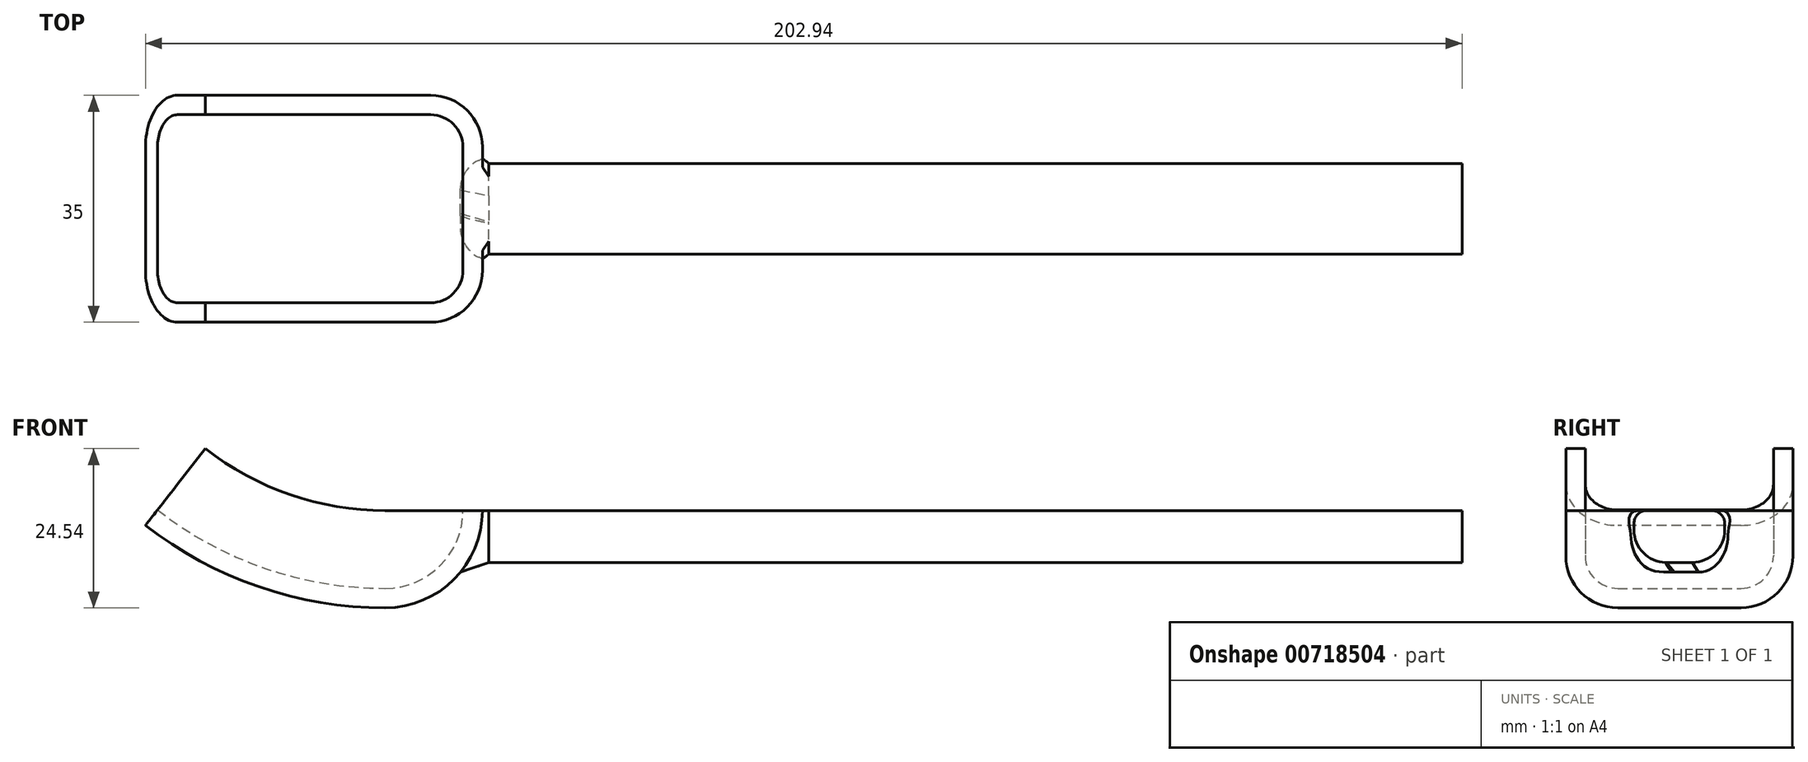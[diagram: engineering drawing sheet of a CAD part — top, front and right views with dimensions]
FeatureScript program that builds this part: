
annotation { "Feature Type Name" : "Feature", "Feature Type Description" : "" }
export const myFeature = defineFeature(function(context is Context, id is Id, definition is map)
    precondition{}
    {
        {
            assignVariable(context, id + "F0", {"variableType" : VariableType.ANGLE, "name" : "Rotation", "angleValue" : 38 * degree});
        }
        {
            assignVariable(context, id + "F1", {"variableType" : VariableType.LENGTH, "name" : "HandleLength", "lengthValue" : 150 * mm});
        }
        {
            assignVariable(context, id + "F2", {"variableType" : VariableType.LENGTH, "name" : "HandleStart", "lengthValue" : 16 * mm});
        }
        {
            var Q0;
            Q0=qCreatedBy(makeId("Right.planeOp"),FACE);
            var sketch = newSketch(context, id + "F3", { "sketchPlane" : qUnion([Q0])});
            skLineSegment(sketch, "E0", {"start": v(0, 0) * mm, "end": v(9.5, 0) * mm});
            skLineSegment(sketch, "E1", {"start": v(0, 0) * mm, "end": v(-9.5, 0) * mm});
            skLineSegment(sketch, "E2", {"start": v(-17.5, 8) * mm, "end": v(-17.5, 15) * mm});
            skLineSegment(sketch, "E3", {"start": v(-17.5, 15) * mm, "end": v(-14.5, 15) * mm});
            skLineSegment(sketch, "E4", {"start": v(-14.5, 15) * mm, "end": v(-14.5, 8) * mm});
            skLineSegment(sketch, "E5", {"start": v(-9.5, 3) * mm, "end": v(9.5, 3) * mm});
            skLineSegment(sketch, "E6", {"start": v(14.5, 8) * mm, "end": v(14.5, 15) * mm});
            skLineSegment(sketch, "E7", {"start": v(14.5, 15) * mm, "end": v(17.5, 15) * mm});
            skLineSegment(sketch, "E8", {"start": v(17.5, 15) * mm, "end": v(17.5, 8) * mm});
            skPoint(sketch, "E9.visualSharp", {"position": v(-14.5, 3) * mm});
            skArc(sketch, "E9.filletArc", {"start": v(-14.5, 8) * mm, "mid": v(-13.04, 4.46) * mm, "end": v(-9.5, 3) * mm});
            skPoint(sketch, "E10.visualSharp", {"position": v(14.5, 3) * mm});
            skArc(sketch, "E10.filletArc", {"start": v(9.5, 3) * mm, "mid": v(13.04, 4.46) * mm, "end": v(14.5, 8) * mm});
            skPoint(sketch, "E11.visualSharp", {"position": v(17.5, 0) * mm});
            skArc(sketch, "E11.filletArc", {"start": v(9.5, 0) * mm, "mid": v(15.16, 2.34) * mm, "end": v(17.5, 8) * mm});
            skPoint(sketch, "E12.visualSharp", {"position": v(-17.5, 0) * mm});
            skArc(sketch, "E12.filletArc", {"start": v(-17.5, 8) * mm, "mid": v(-15.16, 2.34) * mm, "end": v(-9.5, 0) * mm});
            skLineSegment(sketch, "E13", {"start": v(-13.2, 60) * mm, "end": v(15.15, 60) * mm});
            skSolve(sketch);
        }
        {
            var Q0;
            Q0=makeQuery(id+"F3.imprint","IMPRINT",FACE,{"disambiguationData":[TD([[makeQuery(id+"F3.imprint","IMPRINT",EDGE,{"derivedFrom":sQuery(id+"F3.wireOp",EDGE,"E0")}),1.0]])]});
            var Q1;
            Q1=sQuery(id+"F3.wireOp",EDGE,"E13");
            revolve(context, id + "F4", {"surfaceOperationType" : NewSurfaceOperationType.NEW, "entities" : qUnion([Q0]), "axis" : qUnion([Q1]), "revolveType" : RevolveType.ONE_DIRECTION, "angle" : getVariable(context, 'Rotation')});
        }
        {
            var Q0;
            Q0=makeQuery(id+"F4.opRevolve","CAP_FACE",FACE,{"disambiguationData":[OSD([sQuery(id+"F3.wireOp",EDGE,"E0"),sQuery(id+"F3.wireOp",EDGE,"E1"),sQuery(id+"F3.wireOp",EDGE,"E2"),sQuery(id+"F3.wireOp",EDGE,"E3"),sQuery(id+"F3.wireOp",EDGE,"E4"),sQuery(id+"F3.wireOp",EDGE,"E5"),sQuery(id+"F3.wireOp",EDGE,"E6"),sQuery(id+"F3.wireOp",EDGE,"E7"),sQuery(id+"F3.wireOp",EDGE,"E8"),sQuery(id+"F3.wireOp",EDGE,"E9.filletArc"),sQuery(id+"F3.wireOp",EDGE,"E10.filletArc"),sQuery(id+"F3.wireOp",EDGE,"E11.filletArc"),sQuery(id+"F3.wireOp",EDGE,"E12.filletArc")])],"isStart":true});
            var Q1;
            Q1=makeQuery(id+"F4.opRevolve","CAP_EDGE",EDGE,{"disambiguationData":[OSD([sQuery(id+"F3.wireOp",EDGE,"E3")])],"isStart":true});
            revolve(context, id + "F5", {"operationType" : NewBodyOperationType.ADD, "surfaceOperationType" : NewSurfaceOperationType.NEW, "entities" : qUnion([Q0]), "axis" : qUnion([Q1]), "revolveType" : RevolveType.ONE_DIRECTION, "oppositeDirection" : true, "angle" : 90 * degree});
        }
        {
            var Q0;
            Q0=qCreatedBy(makeId("Right.planeOp"),FACE);
            cPlane(context, id + "F6", {"entities" : qUnion([Q0]), "cplaneType" : CPlaneType.OFFSET, "offset" : getVariable(context, 'HandleStart'), "width" : 150 * mm, "height" : 150 * mm});
        }
        {
            var Q0;
            Q0=qCreatedBy(id+"F6.planeOp",FACE);
            var sketch = newSketch(context, id + "F7", { "sketchPlane" : qUnion([Q0])});
            skLineSegment(sketch, "E14", {"start": v(0, 15) * mm, "end": v(5, 15) * mm});
            skLineSegment(sketch, "E15", {"start": v(7, 13) * mm, "end": v(7, 12) * mm});
            skLineSegment(sketch, "E16", {"start": v(2, 7) * mm, "end": v(-2, 7) * mm});
            skLineSegment(sketch, "E17", {"start": v(-7, 12) * mm, "end": v(-7, 13) * mm});
            skLineSegment(sketch, "E18", {"start": v(-5, 15) * mm, "end": v(0, 15) * mm});
            skPoint(sketch, "E19.visualSharp", {"position": v(-7, 15) * mm});
            skArc(sketch, "E19.filletArc", {"start": v(-5, 15) * mm, "mid": v(-6.41, 14.41) * mm, "end": v(-7, 13) * mm});
            skPoint(sketch, "E20.visualSharp", {"position": v(7, 15) * mm});
            skArc(sketch, "E20.filletArc", {"start": v(7, 13) * mm, "mid": v(6.41, 14.41) * mm, "end": v(5, 15) * mm});
            skPoint(sketch, "E21.visualSharp", {"position": v(7, 7) * mm});
            skArc(sketch, "E21.filletArc", {"start": v(2, 7) * mm, "mid": v(5.54, 8.46) * mm, "end": v(7, 12) * mm});
            skPoint(sketch, "E22.visualSharp", {"position": v(-7, 7) * mm});
            skArc(sketch, "E22.filletArc", {"start": v(-7, 12) * mm, "mid": v(-5.54, 8.46) * mm, "end": v(-2, 7) * mm});
            skSolve(sketch);
        }
        {
            var Q0;
            Q0=makeQuery(id+"F5.opRevolve","CAP_EDGE",EDGE,{"disambiguationData":[OSD([sQuery(id+"F3.wireOp",EDGE,"E0"),sQuery(id+"F3.wireOp",EDGE,"E1")])],"isStart":false});
            cPlane(context, id + "F8", {"entities" : qUnion([Q0]), "cplaneType" : CPlaneType.LINE_ANGLE, "offset" : 25 * mm, "angle" : 60 * degree, "width" : 150 * mm, "height" : 150 * mm});
        }
        {
            var Q0;
            Q0=qCreatedBy(id+"F8.planeOp",FACE);
            var sketch = newSketch(context, id + "F9", { "sketchPlane" : qUnion([Q0])});
            skLineSegment(sketch, "E23", {"start": v(0, 8.5) * mm, "end": v(3.4, 8.5) * mm});
            skLineSegment(sketch, "E24", {"start": v(8.4, 13.5) * mm, "end": v(8.4, 18.5) * mm});
            skLineSegment(sketch, "E25", {"start": v(6.4, 20.5) * mm, "end": v(-6.4, 20.5) * mm});
            skLineSegment(sketch, "E26", {"start": v(-8.4, 18.5) * mm, "end": v(-8.4, 13.57) * mm});
            skLineSegment(sketch, "E27", {"start": v(-3.52, 8.57) * mm, "end": v(0, 8.5) * mm});
            skPoint(sketch, "E28.visualSharp", {"position": v(8.4, 8.5) * mm});
            skArc(sketch, "E28.filletArc", {"start": v(3.4, 8.5) * mm, "mid": v(6.94, 9.95) * mm, "end": v(8.4, 13.5) * mm});
            skPoint(sketch, "E29.visualSharp", {"position": v(-8.4, 8.69) * mm});
            skArc(sketch, "E29.filletArc", {"start": v(-8.4, 13.57) * mm, "mid": v(-6.98, 10.08) * mm, "end": v(-3.52, 8.57) * mm});
            skPoint(sketch, "E30.visualSharp", {"position": v(8.4, 20.5) * mm});
            skArc(sketch, "E30.filletArc", {"start": v(8.4, 18.5) * mm, "mid": v(7.81, 19.9) * mm, "end": v(6.4, 20.5) * mm});
            skPoint(sketch, "E31.visualSharp", {"position": v(-8.4, 20.5) * mm});
            skArc(sketch, "E31.filletArc", {"start": v(-6.4, 20.5) * mm, "mid": v(-7.81, 19.9) * mm, "end": v(-8.4, 18.5) * mm});
            skSolve(sketch);
        }
        {
            var Q0;
            Q0 = qSketchRegion(id + "F9", true);
            var Q1;
            Q1=makeQuery(id+"F7.imprint","IMPRINT",FACE,{"disambiguationData":[TD([[makeQuery(id+"F7.imprint","IMPRINT",EDGE,{"derivedFrom":sQuery(id+"F7.wireOp",EDGE,"E14")}),-1.0]])]});
            var Q2;
            Q2=sQuery(id+"F7.wireOp",VERTEX,"E18.start");
            var Q3;
            Q3=sQuery(id+"F9.wireOp",VERTEX,"E25.end");
            loft(context, id + "F10", {"operationType" : NewBodyOperationType.ADD, "sheetProfilesArray" : [{ "sheetProfileEntities" : qUnion([Q0]) }, { "sheetProfileEntities" : qUnion([Q1]) }], "matchVertices" : true, "vertices" : qUnion([Q2, Q3])});
        }
        {
            var Q0;
            Q0 = qSketchRegion(id + "F9", true);
            var Q1;
            Q1 = qSketchRegion(id + "F7", true);
            var Q2;
            Q2=makeQuery(id+"F10.opLoft","MID_CAP_VERTEX",VERTEX,{"disambiguationData":[OSD([sQuery(id+"F7.wireOp",EDGE,"E14"),sQuery(id+"F7.wireOp",EDGE,"E20.filletArc")])],"capPos":1.0});
            var Q3;
            Q3=makeQuery(id+"F10.opLoft","MID_CAP_VERTEX",VERTEX,{"disambiguationData":[OSD([sQuery(id+"F9.wireOp",EDGE,"E25"),sQuery(id+"F9.wireOp",EDGE,"E30.filletArc")])],"capPos":0.0});
            loft(context, id + "F11", {"operationType" : NewBodyOperationType.ADD, "sheetProfilesArray" : [{ "sheetProfileEntities" : qUnion([Q0]) }, { "sheetProfileEntities" : qUnion([Q1]) }], "matchVertices" : true, "vertices" : qUnion([Q2, Q3])});
        }
        {
            var Q0;
            Q0=makeQuery(id+"F10.opLoft","CAP_FACE",FACE,{"disambiguationData":[OSD([makeQuery(id+"F7.imprint","IMPRINT",FACE,{"disambiguationData":[TD([[makeQuery(id+"F7.imprint","IMPRINT",EDGE,{"derivedFrom":sQuery(id+"F7.wireOp",EDGE,"E14")}),-1.0]])]})])],"isStart":true});
            extrude(context, id + "F12", {"entities" : qUnion([Q0]), "operationType" : NewBodyOperationType.ADD, "depth" : getVariable(context, 'HandleLength'), "offsetDistance" : 25 * mm});
        }
    });
